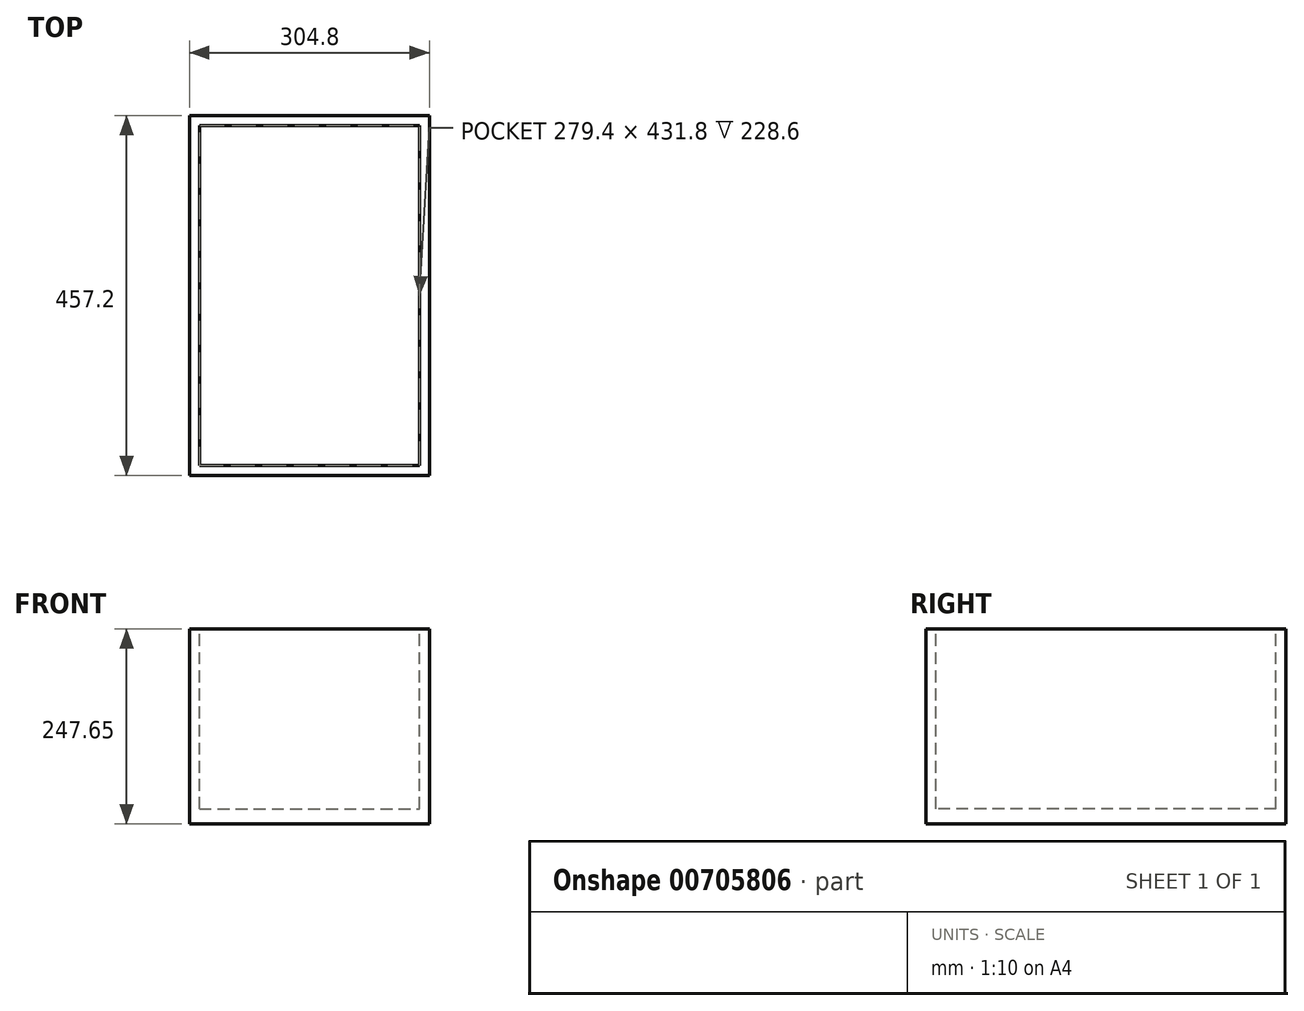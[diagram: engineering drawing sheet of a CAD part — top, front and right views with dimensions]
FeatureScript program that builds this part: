
annotation { "Feature Type Name" : "Feature", "Feature Type Description" : "" }
export const myFeature = defineFeature(function(context is Context, id is Id, definition is map)
    precondition{}
    {
        {
            var Q0;
            Q0=qCreatedBy(makeId("Top.planeOp"),FACE);
            var sketch = newSketch(context, id + "F0", { "sketchPlane" : qUnion([Q0])});
            skLineSegment(sketch, "E0.bottom", {"start": v(152.4, 228.6) * mm, "end": v(-152.4, 228.6) * mm});
            skLineSegment(sketch, "E0.top", {"start": v(152.4, -228.6) * mm, "end": v(-152.4, -228.6) * mm});
            skLineSegment(sketch, "E0.left", {"start": v(152.4, 228.6) * mm, "end": v(152.4, -228.6) * mm});
            skLineSegment(sketch, "E0.right", {"start": v(-152.4, 228.6) * mm, "end": v(-152.4, -228.6) * mm});
            skPoint(sketch, "E0.middle", {"position": v(0, 0) * mm});
            skSolve(sketch);
        }
        {
            var Q0;
            Q0 = qSketchRegion(id + "F0", true);
            extrude(context, id + "F1", {"entities" : qUnion([Q0]), "depth" : 247.65 * mm, "offsetDistance" : 25.4 * mm});
        }
        {
            var Q0;
            Q0=makeQuery(id+"F1.opExtrude","CAP_FACE",FACE,{"disambiguationData":[OSD([sQuery(id+"F0.wireOp",EDGE,"E0.bottom"),sQuery(id+"F0.wireOp",EDGE,"E0.top"),sQuery(id+"F0.wireOp",EDGE,"E0.left"),sQuery(id+"F0.wireOp",EDGE,"E0.right")])],"isStart":false});
            var sketch = newSketch(context, id + "F2", { "sketchPlane" : qUnion([Q0])});
            skLineSegment(sketch, "E1.0", {"start": v(-139.7, -215.9) * mm, "end": v(139.7, -215.9) * mm});
            skLineSegment(sketch, "E1.1", {"start": v(-139.7, 215.9) * mm, "end": v(-139.7, -215.9) * mm});
            skLineSegment(sketch, "E1.2", {"start": v(139.7, 215.9) * mm, "end": v(-139.7, 215.9) * mm});
            skLineSegment(sketch, "E1.3", {"start": v(139.7, -215.9) * mm, "end": v(139.7, 215.9) * mm});
            skSolve(sketch);
        }
        {
            var Q0;
            Q0=makeQuery(id+"F2.imprint","IMPRINT",FACE,{"disambiguationData":[TD([[makeQuery(id+"F2.imprint","IMPRINT",EDGE,{"derivedFrom":sQuery(id+"F2.wireOp",EDGE,"E1.0")}),1.0]])]});
            extrude(context, id + "F3", {"entities" : qUnion([Q0]), "operationType" : NewBodyOperationType.REMOVE, "oppositeDirection" : true, "depth" : 228.6 * mm, "offsetDistance" : 25.4 * mm});
        }
    });
